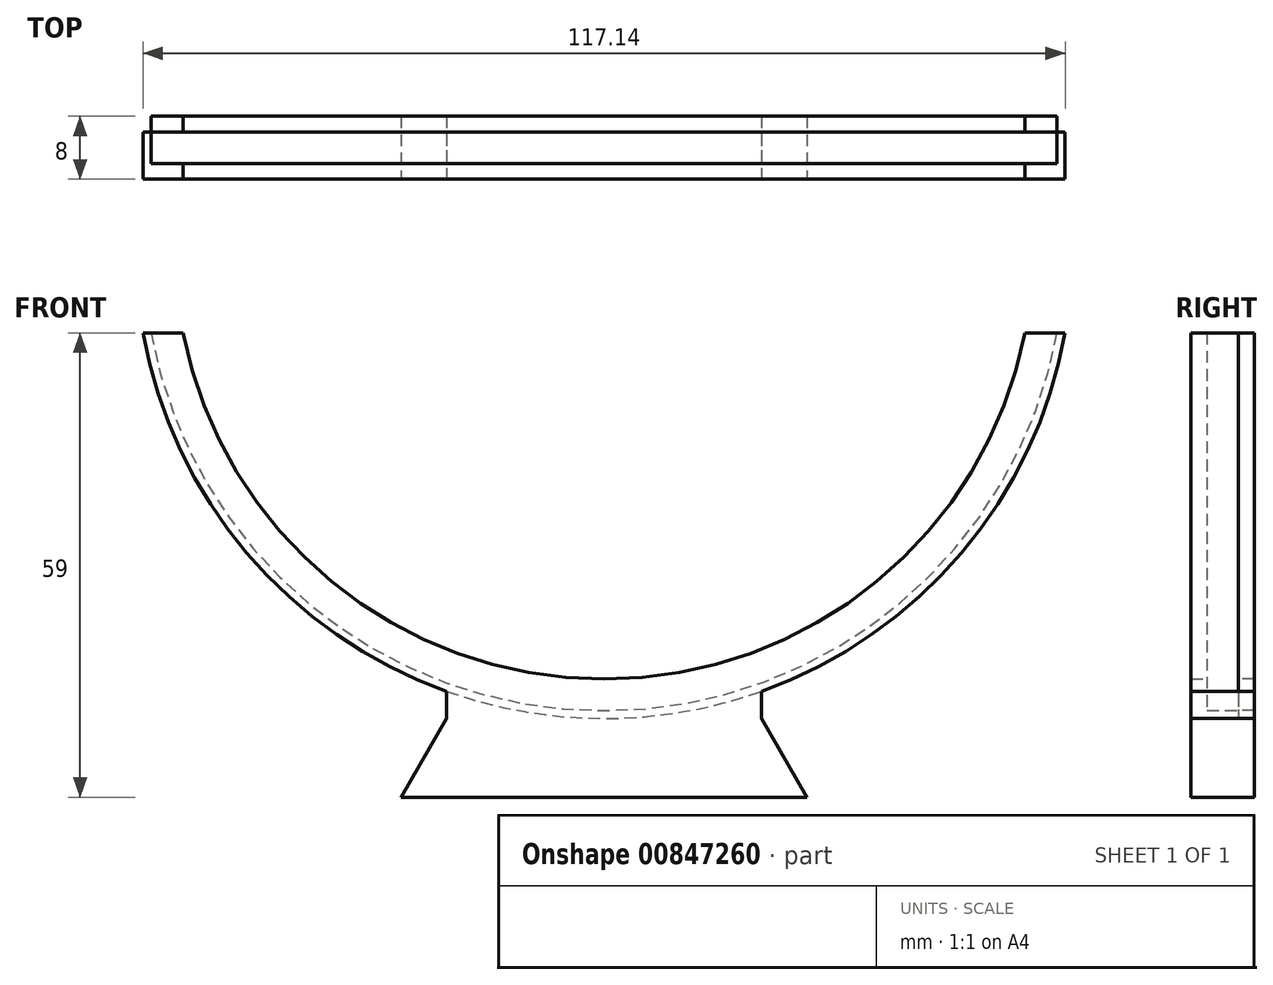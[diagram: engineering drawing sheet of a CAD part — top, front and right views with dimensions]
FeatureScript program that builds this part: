
annotation { "Feature Type Name" : "Feature", "Feature Type Description" : "" }
export const myFeature = defineFeature(function(context is Context, id is Id, definition is map)
    precondition{}
    {
        {
            var Q0;
            Q0=qCreatedBy(makeId("Front.planeOp"),FACE);
            var sketch = newSketch(context, id + "F0", { "sketchPlane" : qUnion([Q0])});
            skCircle(sketch, "E0", {"center": v(0, 0) * mm, "radius": 58.5 * mm});
            skLineSegment(sketch, "E1", {"start": v(0, -58.5) * mm, "end": v(0, -10.5) * mm});
            skLineSegment(sketch, "E2", {"start": v(0, -10.5) * mm, "end": v(57.55, -10.5) * mm});
            skLineSegment(sketch, "E3", {"start": v(0, -10.5) * mm, "end": v(-57.55, -10.5) * mm});
            skCircle(sketch, "E4", {"center": v(0, 0) * mm, "radius": 59.5 * mm});
            skLineSegment(sketch, "E5", {"start": v(-57.55, -10.5) * mm, "end": v(-58.57, -10.5) * mm});
            skLineSegment(sketch, "E6", {"start": v(57.55, -10.5) * mm, "end": v(58.57, -10.5) * mm});
            skSolve(sketch);
        }
        {
            var Q0;
            {var subQ0=sQuery(id+"F0.wireOp",EDGE,"E5");Q0=makeQuery(id+"F0.imprint","IMPRINT",FACE,{"disambiguationData":[TD([[makeQuery(id+"F0.imprint","IMPRINT",EDGE,{"derivedFrom":subQ0}),1.0]])]});}
            extrude(context, id + "F1", {"entities" : qUnion([Q0]), "depth" : 4 * mm, "offsetDistance" : 25 * mm});
        }
        {
            var Q0;
            Q0=makeQuery(id+"F1.opExtrude","CAP_FACE",FACE,{"disambiguationData":[OSD([sQuery(id+"F0.wireOp",EDGE,"E0"),sQuery(id+"F0.wireOp",EDGE,"E4"),sQuery(id+"F0.wireOp",EDGE,"E5"),sQuery(id+"F0.wireOp",EDGE,"E6")])],"isStart":false});
            var sketch = newSketch(context, id + "F2", { "sketchPlane" : qUnion([Q0])});
            skLineSegment(sketch, "E7", {"start": v(-58.57, -10.5) * mm, "end": v(58.57, -10.5) * mm});
            skCircle(sketch, "E8", {"center": v(0, 0) * mm, "radius": 59.5 * mm});
            skCircle(sketch, "E9", {"center": v(0, 0) * mm, "radius": 54.5 * mm});
            skSolve(sketch);
        }
        {
            var Q0;
            {var subQ1=makeQuery(id+"F1.opExtrude","CAP_EDGE",EDGE,{"disambiguationData":[OSD([sQuery(id+"F0.wireOp",EDGE,"E0")])],"isStart":false});Q0=makeQuery(id+"F2.imprint","IMPRINT",FACE,{"disambiguationData":[TD([[makeQuery(id+"F2.imprint","IMPRINT",EDGE,{"derivedFrom":subQ1}),1.0]])]});}
            var Q1;
            {var subQ1=makeQuery(id+"F1.opExtrude","CAP_EDGE",EDGE,{"disambiguationData":[OSD([sQuery(id+"F0.wireOp",EDGE,"E0")])],"isStart":false});Q1=makeQuery(id+"F2.imprint","IMPRINT",FACE,{"disambiguationData":[TD([[makeQuery(id+"F2.imprint","IMPRINT",EDGE,{"derivedFrom":subQ1}),-1.0]])]});}
            extrude(context, id + "F3", {"entities" : qUnion([Q0, Q1]), "operationType" : NewBodyOperationType.ADD, "depth" : 2 * mm, "offsetDistance" : 25 * mm});
        }
        {
            var Q0;
            Q0=makeQuery(id+"F1.opExtrude","CAP_FACE",FACE,{"disambiguationData":[OSD([sQuery(id+"F0.wireOp",EDGE,"E0"),sQuery(id+"F0.wireOp",EDGE,"E4"),sQuery(id+"F0.wireOp",EDGE,"E5"),sQuery(id+"F0.wireOp",EDGE,"E6")])],"isStart":true});
            var sketch = newSketch(context, id + "F4", { "sketchPlane" : qUnion([Q0])});
            skLineSegment(sketch, "E10", {"start": v(-58.57, -10.5) * mm, "end": v(58.57, -10.5) * mm});
            skCircle(sketch, "E11", {"center": v(0, 0) * mm, "radius": 59.5 * mm});
            skCircle(sketch, "E12", {"center": v(0, 0) * mm, "radius": 54.5 * mm});
            skSolve(sketch);
        }
        {
            var Q0;
            {var subQ1=makeQuery(id+"F1.opExtrude","CAP_EDGE",EDGE,{"disambiguationData":[OSD([sQuery(id+"F0.wireOp",EDGE,"E0")])],"isStart":true});Q0=makeQuery(id+"F4.imprint","IMPRINT",FACE,{"disambiguationData":[TD([[makeQuery(id+"F4.imprint","IMPRINT",EDGE,{"derivedFrom":subQ1}),-1.0]])]});}
            var Q1;
            {var subQ2=sQuery(id+"F4.wireOp",EDGE,"E11");Q1=makeQuery(id+"F4.imprint","IMPRINT",FACE,{"disambiguationData":[TD([[makeQuery(id+"F4.imprint","IMPRINT",EDGE,{"disambiguationData":[OD(0.0)],"derivedFrom":subQ2}),-1.0]])]});}
            extrude(context, id + "F5", {"entities" : qUnion([Q0, Q1]), "operationType" : NewBodyOperationType.ADD, "depth" : 2 * mm, "offsetDistance" : 25 * mm});
        }
        {
            var Q0;
            Q0=makeQuery(id+"F3.opExtrude","CAP_FACE",FACE,{"disambiguationData":[OSD([sQuery(id+"F2.wireOp",EDGE,"E7"),sQuery(id+"F2.wireOp",EDGE,"E8"),sQuery(id+"F2.wireOp",EDGE,"E9")])],"isStart":false});
            var sketch = newSketch(context, id + "F6", { "sketchPlane" : qUnion([Q0])});
            skLineSegment(sketch, "E13", {"start": v(0, -59.5) * mm, "end": v(0, -69.5) * mm});
            skLineSegment(sketch, "E14", {"start": v(0, -59.5) * mm, "end": v(-20, -59.5) * mm});
            skLineSegment(sketch, "E15", {"start": v(0, -59.5) * mm, "end": v(20, -59.5) * mm});
            skLineSegment(sketch, "E16", {"start": v(-20, -59.5) * mm, "end": v(-20, -56.04) * mm});
            skLineSegment(sketch, "E17", {"start": v(20, -59.5) * mm, "end": v(20, -56.04) * mm});
            skLineSegment(sketch, "E18", {"start": v(-20, -59.5) * mm, "end": v(-25.77, -69.5) * mm});
            skLineSegment(sketch, "E19", {"start": v(-25.77, -69.5) * mm, "end": v(25.77, -69.5) * mm});
            skLineSegment(sketch, "E20", {"start": v(25.77, -69.5) * mm, "end": v(20, -59.5) * mm});
            skSolve(sketch);
        }
        {
            var Q0;
            {var subQ0=sQuery(id+"F6.wireOp",EDGE,"E13");Q0=makeQuery(id+"F6.imprint","IMPRINT",FACE,{"disambiguationData":[TD([[makeQuery(id+"F6.imprint","IMPRINT",EDGE,{"derivedFrom":subQ0}),1.0]])]});}
            var Q1;
            {var subQ0=sQuery(id+"F6.wireOp",EDGE,"E15");Q1=makeQuery(id+"F6.imprint","IMPRINT",FACE,{"disambiguationData":[TD([[makeQuery(id+"F6.imprint","IMPRINT",EDGE,{"derivedFrom":subQ0}),1.0]])]});}
            var Q2;
            {var subQ0=sQuery(id+"F6.wireOp",EDGE,"E13");Q2=makeQuery(id+"F6.imprint","IMPRINT",FACE,{"disambiguationData":[TD([[makeQuery(id+"F6.imprint","IMPRINT",EDGE,{"derivedFrom":subQ0}),-1.0]])]});}
            var Q3;
            {var subQ0=sQuery(id+"F6.wireOp",EDGE,"E14");Q3=makeQuery(id+"F6.imprint","IMPRINT",FACE,{"disambiguationData":[TD([[makeQuery(id+"F6.imprint","IMPRINT",EDGE,{"derivedFrom":subQ0}),-1.0]])]});}
            extrude(context, id + "F7", {"entities" : qUnion([Q0, Q1, Q2, Q3]), "operationType" : NewBodyOperationType.ADD, "oppositeDirection" : true, "depth" : 8 * mm, "offsetDistance" : 25 * mm});
        }
    });
